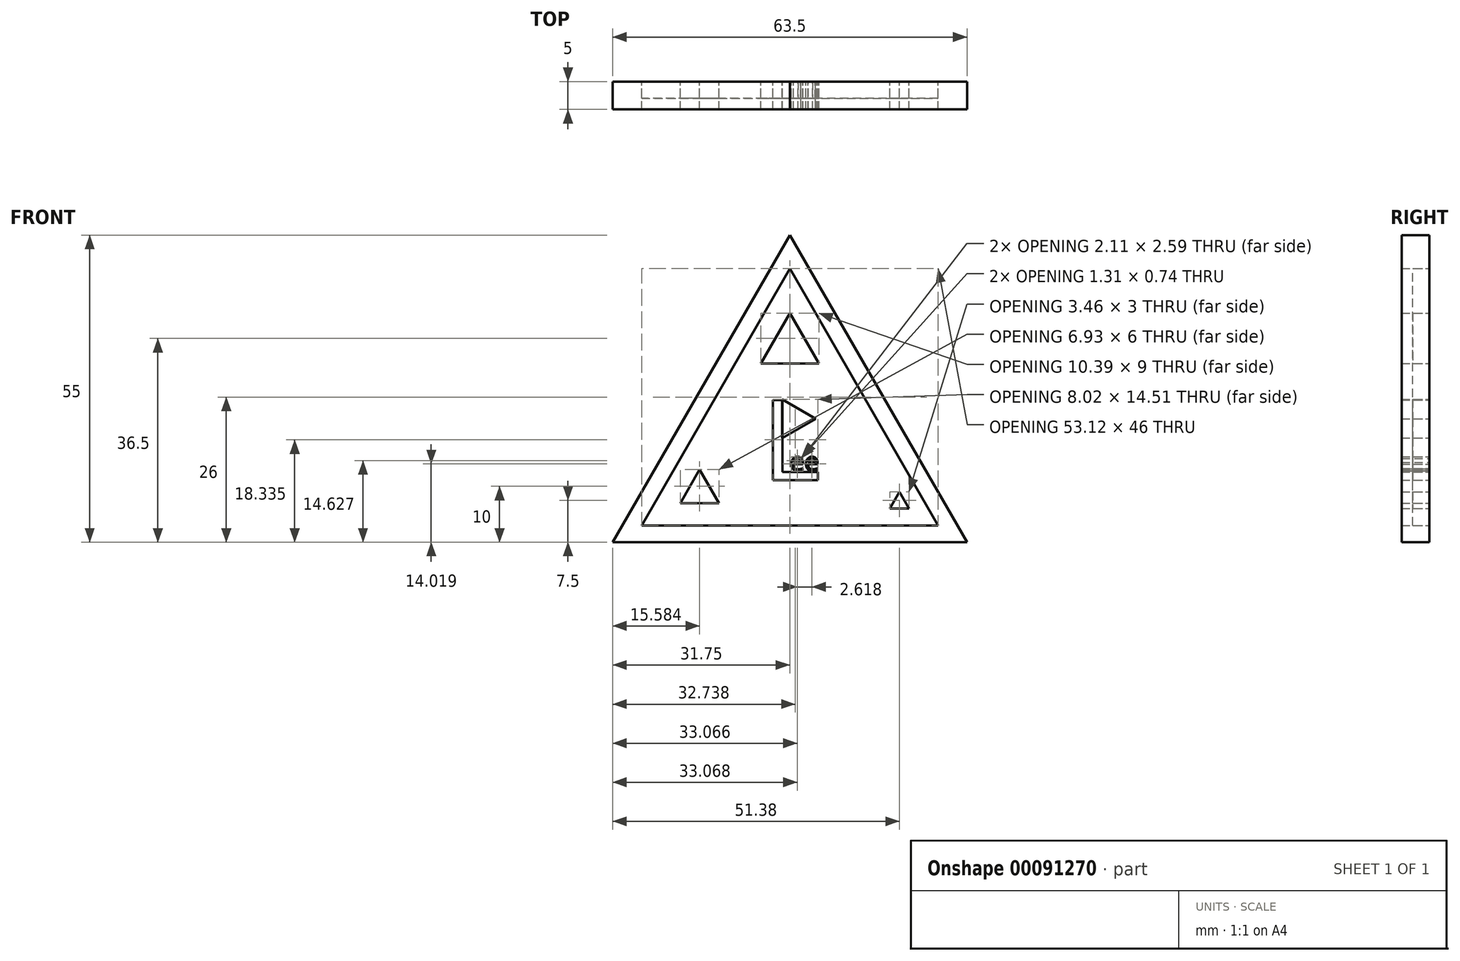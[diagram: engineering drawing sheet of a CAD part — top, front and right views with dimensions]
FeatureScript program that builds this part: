
annotation { "Feature Type Name" : "Feature", "Feature Type Description" : "" }
export const myFeature = defineFeature(function(context is Context, id is Id, definition is map)
    precondition{}
    {
        {
            var Q0;
            Q0=qCreatedBy(makeId("Front.planeOp"),FACE);
            var sketch = newSketch(context, id + "F0", { "sketchPlane" : qUnion([Q0])});
            skLineSegment(sketch, "E0", {"start": v(0, 55) * mm, "end": v(-31.75, 0) * mm});
            skLineSegment(sketch, "E1", {"start": v(31.75, 0) * mm, "end": v(0, 55) * mm});
            skLineSegment(sketch, "E2", {"start": v(-31.75, 0) * mm, "end": v(31.75, 0) * mm});
            skLineSegment(sketch, "E3", {"start": v(0, 49) * mm, "end": v(-26.56, 3) * mm});
            skLineSegment(sketch, "E4", {"start": v(-26.56, 3) * mm, "end": v(26.56, 3) * mm});
            skLineSegment(sketch, "E5", {"start": v(26.56, 3) * mm, "end": v(0, 49) * mm});
            skCircle(sketch, "E6.cCircle", {"center": v(19.63, 7) * mm, "radius": 1 * mm, "construction": true});
            skLineSegment(sketch, "E6.0", {"start": v(21.36, 6) * mm, "end": v(17.9, 6) * mm});
            skLineSegment(sketch, "E6.1", {"start": v(17.9, 6) * mm, "end": v(19.63, 9) * mm});
            skLineSegment(sketch, "E6.2", {"start": v(19.63, 9) * mm, "end": v(21.36, 6) * mm});
            skPoint(sketch, "E6.0.midPoint", {"position": v(19.63, 6) * mm});
            skCircle(sketch, "E7.cCircle", {"center": v(-16.17, 9) * mm, "radius": 2 * mm, "construction": true});
            skLineSegment(sketch, "E7.0", {"start": v(-16.17, 13) * mm, "end": v(-12.7, 7) * mm});
            skLineSegment(sketch, "E7.1", {"start": v(-12.7, 7) * mm, "end": v(-19.63, 7) * mm});
            skLineSegment(sketch, "E7.2", {"start": v(-19.63, 7) * mm, "end": v(-16.17, 13) * mm});
            skPoint(sketch, "E7.0.midPoint", {"position": v(-14.43, 10) * mm});
            skCircle(sketch, "E8.cCircle", {"center": v(0, 35) * mm, "radius": 3 * mm, "construction": true});
            skLineSegment(sketch, "E8.0", {"start": v(5.2, 32) * mm, "end": v(-5.2, 32) * mm});
            skLineSegment(sketch, "E8.1", {"start": v(-5.2, 32) * mm, "end": v(0, 41) * mm});
            skLineSegment(sketch, "E8.2", {"start": v(0, 41) * mm, "end": v(5.2, 32) * mm});
            skPoint(sketch, "E8.0.midPoint", {"position": v(0, 32) * mm});
            skText(sketch, "E9", { "text": "L", "fontName": "OpenSans-Regular.ttf"});
            skLineSegment(sketch, "E10", {"start": v(0, 49) * mm, "end": v(0, 0) * mm, "construction": true});
            skLineSegment(sketch, "E11", {"start": v(-26.56, 3) * mm, "end": v(13.28, 26) * mm, "construction": true});
            skLineSegment(sketch, "E12", {"start": v(-5, 11.08) * mm, "end": v(5, 25.6) * mm, "construction": true});
            skLineSegment(sketch, "E13", {"start": v(5, 11.08) * mm, "end": v(0, 18.33) * mm, "construction": true});
            skText(sketch, "E14", { "text": "ee", "fontName": "OpenSans-Regular.ttf"});
            skCircle(sketch, "E15.cCircle", {"center": v(0.64, 22.13) * mm, "radius": 2 * mm, "construction": true});
            skLineSegment(sketch, "E15.0", {"start": v(4.64, 22.13) * mm, "end": v(-1.36, 18.66) * mm});
            skLineSegment(sketch, "E15.1", {"start": v(-1.36, 18.66) * mm, "end": v(-1.36, 25.6) * mm});
            skLineSegment(sketch, "E15.2", {"start": v(-1.36, 25.6) * mm, "end": v(4.64, 22.13) * mm});
            skPoint(sketch, "E15.0.midPoint", {"position": v(1.64, 20.4) * mm});
            const initialGuessF0  = {"E9": [-0.005, 0.01108, 1, 0, 0.01451], "E14": [0, 0.01277, 1, 0, 0.00336]};
            skSetInitialGuess(sketch, initialGuessF0);
            skSolve(sketch);
        }
        {
            var Q0;
            Q0=makeQuery(id+"F0.imprint","IMPRINT",FACE,{"disambiguationData":[TD([[makeQuery(id+"F0.imprint","IMPRINT",EDGE,{"derivedFrom":sQuery(id+"F0.wireOp",EDGE,"E0")}),1.0]])]});
            var Q1;
            Q1=makeQuery(id+"F0.imprint","IMPRINT",FACE,{"disambiguationData":[TD([[makeQuery(id+"F0.imprint","IMPRINT",EDGE,{"derivedFrom":sQuery(id+"F0.wireOp",EDGE,"E8.0")}),-1.0]])]});
            var Q2;
            Q2=makeQuery(id+"F0.imprint","IMPRINT",FACE,{"disambiguationData":[TD([[makeQuery(id+"F0.imprint","IMPRINT",EDGE,{"derivedFrom":sQuery(id+"F0.wireOp",EDGE,"E7.0")}),-1.0]])]});
            var Q3;
            Q3=makeQuery(id+"F0.imprint","IMPRINT",FACE,{"disambiguationData":[TD([[makeQuery(id+"F0.imprint","IMPRINT",EDGE,{"derivedFrom":sQuery(id+"F0.wireOp",EDGE,"E6.0")}),-1.0]])]});
            var Q4;
            {var subQ0=sQuery(id+"F0.wireOp",EDGE,"E15.2");Q4=makeQuery(id+"F0.imprint","IMPRINT",FACE,{"disambiguationData":[TD([[makeQuery(id+"F0.imprint","IMPRINT",EDGE,{"derivedFrom":subQ0}),-1.0]])]});}
            var Q5;
            {var subQ5=sQuery(id+"F0.wireOp",EDGE,"E9.sketch_text.stroke-0");Q5=makeQuery(id+"F0.imprint","IMPRINT",FACE,{"disambiguationData":[TD([[makeQuery(id+"F0.imprint","IMPRINT",EDGE,{"derivedFrom":subQ5}),-1.0]])]});}
            var Q6;
            Q6=makeQuery(id+"F0.imprint","IMPRINT",FACE,{"disambiguationData":[TD([[makeQuery(id+"F0.imprint","IMPRINT",EDGE,{"derivedFrom":sQuery(id+"F0.wireOp",EDGE,"E14.sketch_text.stroke-0")}),-1.0]])]});
            var Q7;
            Q7=makeQuery(id+"F0.imprint","IMPRINT",FACE,{"disambiguationData":[TD([[makeQuery(id+"F0.imprint","IMPRINT",EDGE,{"derivedFrom":sQuery(id+"F0.wireOp",EDGE,"E14.sketch_text.stroke-19")}),-1.0]])]});
            extrude(context, id + "F1", {"entities" : qUnion([Q0, Q1, Q2, Q3, Q4, Q5, Q6, Q7]), "depth" : 5 * mm});
        }
        {
            var Q0;
            Q0=makeQuery(id+"F0.imprint","IMPRINT",FACE,{"disambiguationData":[TD([[makeQuery(id+"F0.imprint","IMPRINT",EDGE,{"derivedFrom":sQuery(id+"F0.wireOp",EDGE,"E3")}),1.0]])]});
            extrude(context, id + "F2", {"entities" : qUnion([Q0]), "depth" : 3 * mm});
        }
    });
